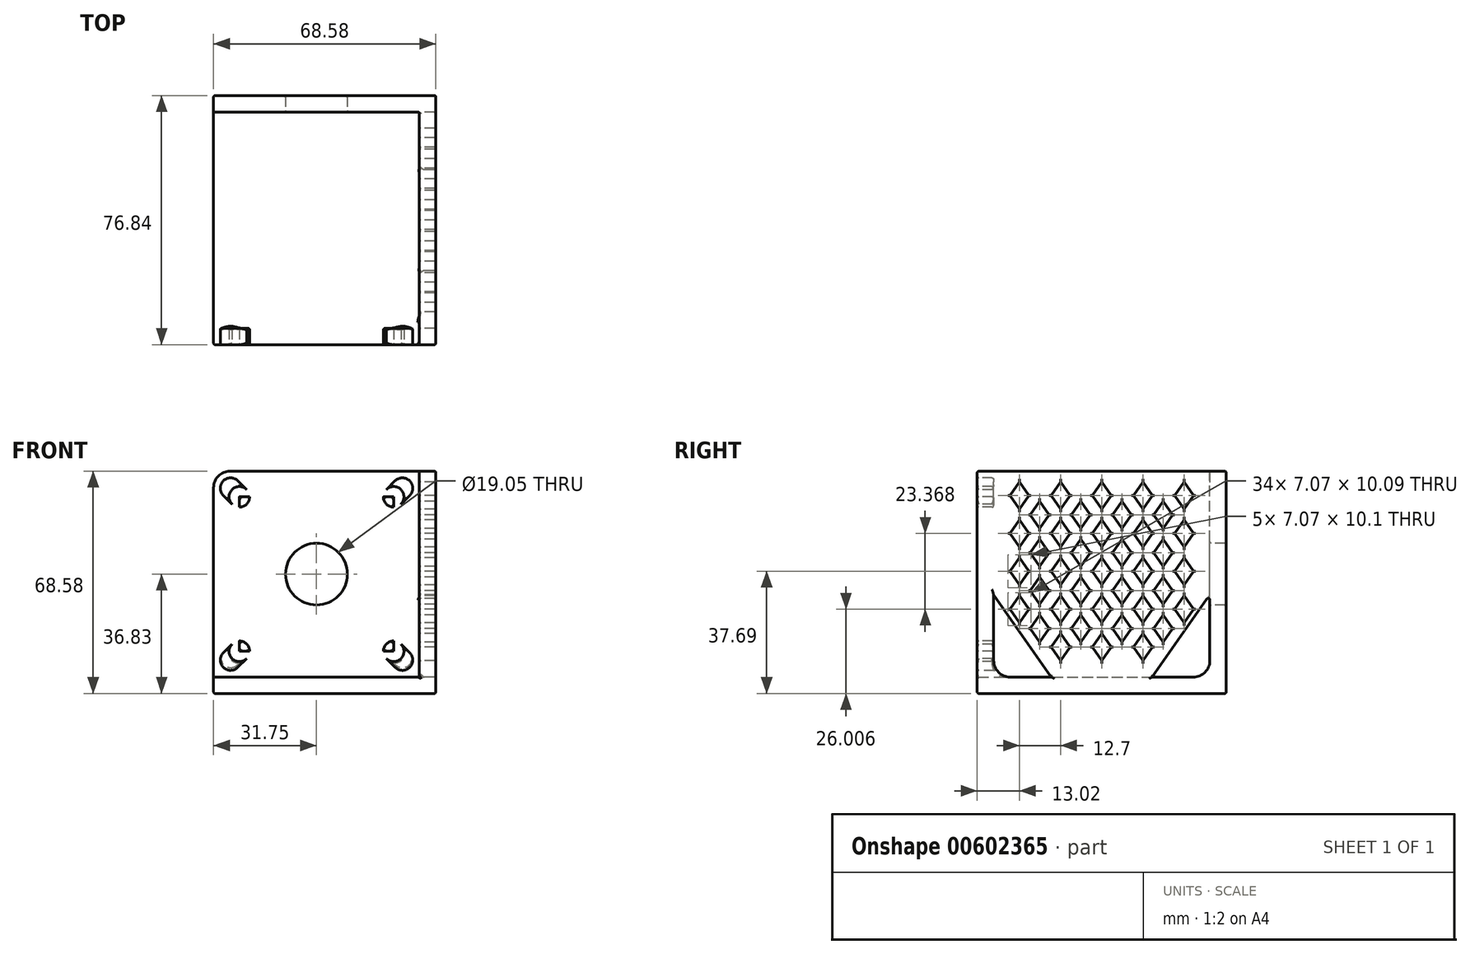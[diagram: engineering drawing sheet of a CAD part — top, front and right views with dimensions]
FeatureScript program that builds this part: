
annotation { "Feature Type Name" : "Feature", "Feature Type Description" : "" }
export const myFeature = defineFeature(function(context is Context, id is Id, definition is map)
    precondition{}
    {
        {
            var Q0;
            Q0=qCreatedBy(makeId("Right.planeOp"),FACE);
            var sketch = newSketch(context, id + "F0", { "sketchPlane" : qUnion([Q0])});
            skLineSegment(sketch, "E0", {"start": v(0, 0) * mm, "end": v(33.34, 0) * mm});
            skLineSegment(sketch, "E1", {"start": v(33.34, 0) * mm, "end": v(33.34, 63.5) * mm});
            skLineSegment(sketch, "E2", {"start": v(33.34, 63.5) * mm, "end": v(38.42, 63.5) * mm});
            skLineSegment(sketch, "E3", {"start": v(38.42, 63.5) * mm, "end": v(38.42, -5.08) * mm});
            skLineSegment(sketch, "E4", {"start": v(38.42, -5.08) * mm, "end": v(0, -5.08) * mm});
            skLineSegment(sketch, "E5", {"start": v(0, -5.08) * mm, "end": v(0, 0) * mm});
            skLineSegment(sketch, "E6.MirrorCS", {"start": v(-33.34, 0) * mm, "end": v(-33.34, 63.5) * mm});
            skLineSegment(sketch, "E7.MirrorCS", {"start": v(0, 0) * mm, "end": v(-33.34, 0) * mm});
            skLineSegment(sketch, "E8.MirrorCS", {"start": v(-38.42, -5.08) * mm, "end": v(0, -5.08) * mm});
            skLineSegment(sketch, "E9.MirrorCS", {"start": v(-38.42, 63.5) * mm, "end": v(-38.42, -5.08) * mm});
            skLineSegment(sketch, "E10.MirrorCS", {"start": v(-33.34, 63.5) * mm, "end": v(-38.42, 63.5) * mm});
            skSolve(sketch);
        }
        {
            var Q0;
            Q0=makeQuery(id+"F0.imprint","IMPRINT",FACE,{"disambiguationData":[TD([[makeQuery(id+"F0.imprint","IMPRINT",EDGE,{"derivedFrom":sQuery(id+"F0.wireOp",EDGE,"E0")}),-1.0]])]});
            var Q1;
            Q1=makeQuery(id+"F0.imprint","IMPRINT",FACE,{"disambiguationData":[TD([[makeQuery(id+"F0.imprint","IMPRINT",EDGE,{"derivedFrom":sQuery(id+"F0.wireOp",EDGE,"E5")}),1.0]])]});
            extrude(context, id + "F1", {"entities" : qUnion([Q0, Q1]), "endBound" : BoundingType.SYMMETRIC, "depth" : 63.5 * mm, "offsetDistance" : 25.4 * mm});
        }
        {
            var Q0;
            Q0=makeQuery(id+"F1.opExtrude","CAP_FACE",FACE,{"disambiguationData":[OSD([sQuery(id+"F0.wireOp",EDGE,"E0"),sQuery(id+"F0.wireOp",EDGE,"E1"),sQuery(id+"F0.wireOp",EDGE,"E2"),sQuery(id+"F0.wireOp",EDGE,"E3"),sQuery(id+"F0.wireOp",EDGE,"E4"),sQuery(id+"F0.wireOp",EDGE,"E6.MirrorCS"),sQuery(id+"F0.wireOp",EDGE,"E7.MirrorCS"),sQuery(id+"F0.wireOp",EDGE,"E8.MirrorCS"),sQuery(id+"F0.wireOp",EDGE,"E9.MirrorCS"),sQuery(id+"F0.wireOp",EDGE,"E10.MirrorCS")])],"isStart":false});
            var sketch = newSketch(context, id + "F2", { "sketchPlane" : qUnion([Q0])});
            skLineSegment(sketch, "E11.bottom", {"start": v(-38.42, 63.5) * mm, "end": v(38.42, 63.5) * mm});
            skLineSegment(sketch, "E11.top", {"start": v(-38.42, -5.08) * mm, "end": v(38.42, -5.08) * mm});
            skLineSegment(sketch, "E11.left", {"start": v(-38.42, 63.5) * mm, "end": v(-38.42, -5.08) * mm});
            skLineSegment(sketch, "E11.right", {"start": v(38.42, 63.5) * mm, "end": v(38.42, -5.08) * mm});
            skSolve(sketch);
        }
        {
            var Q0;
            {var subQ3=sQuery(id+"F0.wireOp",EDGE,"E1");var subQ6=makeQuery(id+"F1.opExtrude","CAP_EDGE",EDGE,{"disambiguationData":[OSD([subQ3])],"isStart":false});Q0=makeQuery(id+"F2.imprint","IMPRINT",FACE,{"disambiguationData":[TD([[makeQuery(id+"F2.imprint","IMPRINT",EDGE,{"derivedFrom":subQ6}),1.0]])]});}
            var Q1;
            Q1=makeQuery(id+"F2.imprint","IMPRINT",FACE,{"disambiguationData":[TD([[makeQuery(id+"F2.imprint","IMPRINT",EDGE,{"derivedFrom":sQuery(id+"F2.wireOp",EDGE,"E11.top")}),-1.0]])]});
            extrude(context, id + "F3", {"entities" : qUnion([Q0, Q1]), "operationType" : NewBodyOperationType.ADD, "depth" : 5.08 * mm, "offsetDistance" : 25.4 * mm});
        }
        {
            var Q0;
            Q0=makeQuery(id+"F1.opExtrude","SWEPT_EDGE",EDGE,{"disambiguationData":[OSD([sQuery(id+"F0.wireOp",EDGE,"E0"),sQuery(id+"F0.wireOp",EDGE,"E1")])]});
            var Q1;
            Q1=makeQuery(id+"F1.opExtrude","SWEPT_EDGE",EDGE,{"disambiguationData":[OSD([sQuery(id+"F0.wireOp",EDGE,"E6.MirrorCS"),sQuery(id+"F0.wireOp",EDGE,"E7.MirrorCS")])]});
            var Q2;
            Q2=makeQuery(id+"F1.opExtrude","CAP_EDGE",EDGE,{"disambiguationData":[OSD([sQuery(id+"F0.wireOp",EDGE,"E0"),sQuery(id+"F0.wireOp",EDGE,"E7.MirrorCS")])],"isStart":false});
            fillet(context, id + "F4", {"entities" : qUnion([Q0, Q1, Q2]), "radius" : 5.08 * mm, "tangentPropagation" : true, "allowEdgeOverflow" : false});
        }
        {
            var Q0;
            Q0=makeQuery(id+"F1.opExtrude","SWEPT_FACE",FACE,{"disambiguationData":[OSD([sQuery(id+"F0.wireOp",EDGE,"E9.MirrorCS")])]});
            var sketch = newSketch(context, id + "F5", { "sketchPlane" : qUnion([Q0])});
            skLineSegment(sketch, "E12.0", {"start": v(31.75, 0) * mm, "end": v(-31.75, 0) * mm});
            skLineSegment(sketch, "E13.0.0", {"start": v(-31.75, 63.5) * mm, "end": v(-31.75, -5.08) * mm});
            skLineSegment(sketch, "E13.0.1", {"start": v(-31.75, -5.08) * mm, "end": v(31.75, -5.08) * mm});
            skLineSegment(sketch, "E13.0.2", {"start": v(31.75, -5.08) * mm, "end": v(31.75, 63.5) * mm});
            skLineSegment(sketch, "E13.0.3", {"start": v(31.75, 63.5) * mm, "end": v(-31.75, 63.5) * mm});
            skPoint(sketch, "E14", {"position": v(0, 31.75) * mm});
            skCircle(sketch, "E15", {"center": v(0, 31.75) * mm, "radius": 19.84 * mm});
            skCircle(sketch, "E16", {"center": v(0, 31.75) * mm, "radius": 9.53 * mm});
            skSolve(sketch);
        }
        {
            var Q0;
            Q0=makeQuery(id+"F5.imprint","IMPRINT",FACE,{"disambiguationData":[TD([[makeQuery(id+"F5.imprint","IMPRINT",EDGE,{"derivedFrom":sQuery(id+"F5.wireOp",EDGE,"E16")}),1.0]])]});
            extrude(context, id + "F6", {"entities" : qUnion([Q0]), "operationType" : NewBodyOperationType.REMOVE, "endBound" : BoundingType.THROUGH_ALL, "oppositeDirection" : true, "depth" : 25.4 * mm, "offsetDistance" : 25.4 * mm});
        }
        {
            var Q0;
            Q0=makeQuery(id+"F5.imprint","IMPRINT",FACE,{"disambiguationData":[TD([[makeQuery(id+"F5.imprint","IMPRINT",EDGE,{"derivedFrom":sQuery(id+"F5.wireOp",EDGE,"E15")}),1.0]])]});
            extrude(context, id + "F7", {"entities" : qUnion([Q0]), "operationType" : NewBodyOperationType.REMOVE, "oppositeDirection" : true, "depth" : 25.4 * mm, "offsetDistance" : 25.4 * mm});
        }
        {
            var Q0;
            {var subQ2=sQuery(id+"F5.wireOp",EDGE,"E12.0");Q0=makeQuery(id+"F5.imprint","IMPRINT",FACE,{"disambiguationData":[TD([[makeQuery(id+"F5.imprint","IMPRINT",EDGE,{"derivedFrom":subQ2}),-1.0]])]});}
            var sketch = newSketch(context, id + "F8", { "sketchPlane" : qUnion([Q0])});
            skLineSegment(sketch, "E17", {"start": v(-23.81, 55.56) * mm, "end": v(23.81, 55.56) * mm});
            skPoint(sketch, "E18", {"position": v(0, 55.56) * mm});
            skLineSegment(sketch, "E19", {"start": v(-23.81, 55.56) * mm, "end": v(-23.81, 7.94) * mm});
            skPoint(sketch, "E20", {"position": v(-23.81, 31.75) * mm});
            skPoint(sketch, "E21.0", {"position": v(0, 31.75) * mm});
            skLineSegment(sketch, "E22", {"start": v(0, 31.75) * mm, "end": v(-34.13, 31.75) * mm});
            skLineSegment(sketch, "E23.MirrorCS", {"start": v(-23.81, 7.94) * mm, "end": v(23.81, 7.94) * mm});
            skLineSegment(sketch, "E24.MirrorCS", {"start": v(23.81, 55.56) * mm, "end": v(23.81, 7.94) * mm});
            skLineSegment(sketch, "E25", {"start": v(-23.81, 55.56) * mm, "end": v(-19.32, 51.07) * mm});
            skPoint(sketch, "E26", {"position": v(-19.32, 51.07) * mm});
            skLineSegment(sketch, "E27", {"start": v(-23.81, 55.56) * mm, "end": v(-26.5, 58.26) * mm});
            skLineSegment(sketch, "E28.MirrorCS", {"start": v(23.81, 55.56) * mm, "end": v(19.32, 51.07) * mm});
            skLineSegment(sketch, "E29.MirrorCS", {"start": v(23.81, 55.56) * mm, "end": v(26.5, 58.26) * mm});
            skLineSegment(sketch, "E30.MirrorCS", {"start": v(-23.81, 7.94) * mm, "end": v(-26.5, 5.24) * mm});
            skLineSegment(sketch, "E31.MirrorCS", {"start": v(-23.81, 7.94) * mm, "end": v(-19.32, 12.43) * mm});
            skLineSegment(sketch, "E32.MirrorCS", {"start": v(23.81, 7.94) * mm, "end": v(26.5, 5.24) * mm});
            skLineSegment(sketch, "E33.MirrorCS", {"start": v(23.81, 7.94) * mm, "end": v(19.32, 12.43) * mm});
            skArc(sketch, "E34.0.startCap", {"start": v(-21.57, 57.8) * mm, "mid": v(-21.57, 53.32) * mm, "end": v(-26.06, 53.32) * mm});
            skArc(sketch, "E34.0.endCap", {"start": v(-28.75, 56.01) * mm, "mid": v(-28.75, 60.5) * mm, "end": v(-24.26, 60.5) * mm});
            skLineSegment(sketch, "E34.0.left", {"start": v(-26.06, 53.32) * mm, "end": v(-28.75, 56.01) * mm});
            skLineSegment(sketch, "E34.0.right", {"start": v(-21.57, 57.8) * mm, "end": v(-24.26, 60.5) * mm});
            skArc(sketch, "E34.1.startCap", {"start": v(-26.06, 53.32) * mm, "mid": v(-26.06, 57.8) * mm, "end": v(-21.57, 57.8) * mm});
            skArc(sketch, "E34.1.endCap", {"start": v(-17.08, 53.32) * mm, "mid": v(-17.08, 48.83) * mm, "end": v(-21.57, 48.83) * mm});
            skLineSegment(sketch, "E34.1.left", {"start": v(-21.57, 57.8) * mm, "end": v(-17.08, 53.32) * mm});
            skLineSegment(sketch, "E34.1.right", {"start": v(-26.06, 53.32) * mm, "end": v(-21.57, 48.83) * mm});
            skArc(sketch, "E34.2.startCap", {"start": v(26.06, 53.32) * mm, "mid": v(21.57, 53.32) * mm, "end": v(21.57, 57.8) * mm});
            skArc(sketch, "E34.2.endCap", {"start": v(24.26, 60.5) * mm, "mid": v(28.75, 60.5) * mm, "end": v(28.75, 56.01) * mm});
            skLineSegment(sketch, "E34.2.left", {"start": v(21.57, 57.8) * mm, "end": v(24.26, 60.5) * mm});
            skLineSegment(sketch, "E34.2.right", {"start": v(26.06, 53.32) * mm, "end": v(28.75, 56.01) * mm});
            skArc(sketch, "E34.3.startCap", {"start": v(21.57, 57.8) * mm, "mid": v(26.06, 57.8) * mm, "end": v(26.06, 53.32) * mm});
            skArc(sketch, "E34.3.endCap", {"start": v(21.57, 48.83) * mm, "mid": v(17.08, 48.83) * mm, "end": v(17.08, 53.32) * mm});
            skLineSegment(sketch, "E34.3.left", {"start": v(26.06, 53.32) * mm, "end": v(21.57, 48.83) * mm});
            skLineSegment(sketch, "E34.3.right", {"start": v(21.57, 57.8) * mm, "end": v(17.08, 53.32) * mm});
            skArc(sketch, "E34.4.startCap", {"start": v(26.06, 10.18) * mm, "mid": v(26.06, 5.7) * mm, "end": v(21.57, 5.7) * mm});
            skArc(sketch, "E34.4.endCap", {"start": v(17.08, 10.18) * mm, "mid": v(17.08, 14.67) * mm, "end": v(21.57, 14.67) * mm});
            skLineSegment(sketch, "E34.4.left", {"start": v(21.57, 5.7) * mm, "end": v(17.08, 10.18) * mm});
            skLineSegment(sketch, "E34.4.right", {"start": v(26.06, 10.18) * mm, "end": v(21.57, 14.67) * mm});
            skArc(sketch, "E34.5.startCap", {"start": v(21.57, 5.7) * mm, "mid": v(21.57, 10.18) * mm, "end": v(26.06, 10.18) * mm});
            skArc(sketch, "E34.5.endCap", {"start": v(28.75, 7.49) * mm, "mid": v(28.75, 3) * mm, "end": v(24.26, 3) * mm});
            skLineSegment(sketch, "E34.5.left", {"start": v(26.06, 10.18) * mm, "end": v(28.75, 7.49) * mm});
            skLineSegment(sketch, "E34.5.right", {"start": v(21.57, 5.7) * mm, "end": v(24.26, 3) * mm});
            skArc(sketch, "E34.6.startCap", {"start": v(-21.57, 5.7) * mm, "mid": v(-26.06, 5.7) * mm, "end": v(-26.06, 10.18) * mm});
            skArc(sketch, "E34.6.endCap", {"start": v(-21.57, 14.67) * mm, "mid": v(-17.08, 14.67) * mm, "end": v(-17.08, 10.18) * mm});
            skLineSegment(sketch, "E34.6.left", {"start": v(-26.06, 10.18) * mm, "end": v(-21.57, 14.67) * mm});
            skLineSegment(sketch, "E34.6.right", {"start": v(-21.57, 5.7) * mm, "end": v(-17.08, 10.18) * mm});
            skArc(sketch, "E34.7.startCap", {"start": v(-26.06, 10.18) * mm, "mid": v(-21.57, 10.18) * mm, "end": v(-21.57, 5.7) * mm});
            skArc(sketch, "E34.7.endCap", {"start": v(-24.26, 3) * mm, "mid": v(-28.75, 3) * mm, "end": v(-28.75, 7.49) * mm});
            skLineSegment(sketch, "E34.7.left", {"start": v(-21.57, 5.7) * mm, "end": v(-24.26, 3) * mm});
            skLineSegment(sketch, "E34.7.right", {"start": v(-26.06, 10.18) * mm, "end": v(-28.75, 7.49) * mm});
            skSolve(sketch);
        }
        {
            var Q0;
            {var subQ1=sQuery(id+"F8.wireOp",EDGE,"E17");var subQ3=sQuery(id+"F8.wireOp",EDGE,"E34.0.startCap");var subQ4=makeQuery(id+"F8.imprint","INTERSECT",VERTEX,{"derivedFrom":[subQ1,subQ3]});Q0=makeQuery(id+"F8.imprint","IMPRINT",FACE,{"disambiguationData":[TD([[makeQuery(id+"F8.imprint","IMPRINT",EDGE,{"disambiguationData":[TD([[subQ4,1.0]])],"derivedFrom":subQ1}),1.0]])]});}
            var Q1;
            {var subQ1=sQuery(id+"F8.wireOp",EDGE,"E19");var subQ3=sQuery(id+"F8.wireOp",EDGE,"E34.0.startCap");var subQ4=makeQuery(id+"F8.imprint","INTERSECT",VERTEX,{"derivedFrom":[subQ1,subQ3]});Q1=makeQuery(id+"F8.imprint","IMPRINT",FACE,{"disambiguationData":[TD([[makeQuery(id+"F8.imprint","IMPRINT",EDGE,{"disambiguationData":[TD([[subQ4,1.0]])],"derivedFrom":subQ1}),-1.0]])]});}
            var Q2;
            {var subQ0=sQuery(id+"F8.wireOp",EDGE,"E25");var subQ3=sQuery(id+"F8.wireOp",EDGE,"E34.0.startCap");var subQ5=makeQuery(id+"F8.imprint","INTERSECT",VERTEX,{"derivedFrom":[subQ0,subQ3]});Q2=makeQuery(id+"F8.imprint","IMPRINT",FACE,{"disambiguationData":[TD([[makeQuery(id+"F8.imprint","IMPRINT",EDGE,{"disambiguationData":[TD([[subQ5,1.0]])],"derivedFrom":subQ3}),-1.0]])]});}
            var Q3;
            {var subQ0=sQuery(id+"F8.wireOp",EDGE,"E25");var subQ3=sQuery(id+"F8.wireOp",EDGE,"E34.0.startCap");var subQ5=makeQuery(id+"F8.imprint","INTERSECT",VERTEX,{"derivedFrom":[subQ0,subQ3]});Q3=makeQuery(id+"F8.imprint","IMPRINT",FACE,{"disambiguationData":[TD([[makeQuery(id+"F8.imprint","IMPRINT",EDGE,{"disambiguationData":[TD([[subQ5,-1.0]])],"derivedFrom":subQ3}),-1.0]])]});}
            var Q4;
            {var subQ7=sQuery(id+"F8.wireOp",EDGE,"E34.1.endCap");Q4=makeQuery(id+"F8.imprint","IMPRINT",FACE,{"disambiguationData":[TD([[makeQuery(id+"F8.imprint","IMPRINT",EDGE,{"derivedFrom":subQ7}),-1.0]])]});}
            var Q5;
            {var subQ0=sQuery(id+"F8.wireOp",EDGE,"E34.0.startCap");var subQ1=sQuery(id+"F8.wireOp",EDGE,"E17");var subQ2=makeQuery(id+"F8.imprint","INTERSECT",VERTEX,{"derivedFrom":[subQ1,subQ0]});Q5=makeQuery(id+"F8.imprint","IMPRINT",FACE,{"disambiguationData":[TD([[makeQuery(id+"F8.imprint","IMPRINT",EDGE,{"disambiguationData":[TD([[subQ2,-1.0]])],"derivedFrom":subQ1}),1.0]])]});}
            var Q6;
            {var subQ0=sQuery(id+"F8.wireOp",EDGE,"E34.0.startCap");var subQ1=sQuery(id+"F8.wireOp",EDGE,"E19");var subQ2=makeQuery(id+"F8.imprint","INTERSECT",VERTEX,{"derivedFrom":[subQ1,subQ0]});Q6=makeQuery(id+"F8.imprint","IMPRINT",FACE,{"disambiguationData":[TD([[makeQuery(id+"F8.imprint","IMPRINT",EDGE,{"disambiguationData":[TD([[subQ2,-1.0]])],"derivedFrom":subQ1}),-1.0]])]});}
            var Q7;
            Q7=makeQuery(id+"F8.imprint","IMPRINT",FACE,{"disambiguationData":[TD([[makeQuery(id+"F8.imprint","IMPRINT",EDGE,{"derivedFrom":sQuery(id+"F8.wireOp",EDGE,"E34.0.endCap")}),-1.0]])]});
            var Q8;
            Q8=makeQuery(id+"F8.imprint","IMPRINT",FACE,{"disambiguationData":[TD([[makeQuery(id+"F8.imprint","IMPRINT",EDGE,{"derivedFrom":sQuery(id+"F8.wireOp",EDGE,"E34.2.endCap")}),-1.0]])]});
            var Q9;
            {var subQ1=sQuery(id+"F8.wireOp",EDGE,"E24.MirrorCS");var subQ3=sQuery(id+"F8.wireOp",EDGE,"E34.2.startCap");var subQ4=makeQuery(id+"F8.imprint","INTERSECT",VERTEX,{"derivedFrom":[subQ1,subQ3]});Q9=makeQuery(id+"F8.imprint","IMPRINT",FACE,{"disambiguationData":[TD([[makeQuery(id+"F8.imprint","IMPRINT",EDGE,{"disambiguationData":[TD([[subQ4,1.0]])],"derivedFrom":subQ1}),1.0]])]});}
            var Q10;
            {var subQ1=sQuery(id+"F8.wireOp",EDGE,"E17");var subQ3=sQuery(id+"F8.wireOp",EDGE,"E34.2.startCap");var subQ4=makeQuery(id+"F8.imprint","INTERSECT",VERTEX,{"derivedFrom":[subQ1,subQ3]});Q10=makeQuery(id+"F8.imprint","IMPRINT",FACE,{"disambiguationData":[TD([[makeQuery(id+"F8.imprint","IMPRINT",EDGE,{"disambiguationData":[TD([[subQ4,-1.0]])],"derivedFrom":subQ1}),1.0]])]});}
            var Q11;
            {var subQ0=sQuery(id+"F8.wireOp",EDGE,"E28.MirrorCS");var subQ3=sQuery(id+"F8.wireOp",EDGE,"E34.2.startCap");var subQ5=makeQuery(id+"F8.imprint","INTERSECT",VERTEX,{"derivedFrom":[subQ0,subQ3]});Q11=makeQuery(id+"F8.imprint","IMPRINT",FACE,{"disambiguationData":[TD([[makeQuery(id+"F8.imprint","IMPRINT",EDGE,{"disambiguationData":[TD([[subQ5,-1.0]])],"derivedFrom":subQ3}),-1.0]])]});}
            var Q12;
            {var subQ5=sQuery(id+"F8.wireOp",EDGE,"E34.3.endCap");Q12=makeQuery(id+"F8.imprint","IMPRINT",FACE,{"disambiguationData":[TD([[makeQuery(id+"F8.imprint","IMPRINT",EDGE,{"derivedFrom":subQ5}),-1.0]])]});}
            var Q13;
            {var subQ0=sQuery(id+"F8.wireOp",EDGE,"E34.2.startCap");var subQ1=sQuery(id+"F8.wireOp",EDGE,"E24.MirrorCS");var subQ2=makeQuery(id+"F8.imprint","INTERSECT",VERTEX,{"derivedFrom":[subQ1,subQ0]});Q13=makeQuery(id+"F8.imprint","IMPRINT",FACE,{"disambiguationData":[TD([[makeQuery(id+"F8.imprint","IMPRINT",EDGE,{"disambiguationData":[TD([[subQ2,-1.0]])],"derivedFrom":subQ1}),1.0]])]});}
            var Q14;
            {var subQ0=sQuery(id+"F8.wireOp",EDGE,"E34.3.right");var subQ1=sQuery(id+"F8.wireOp",EDGE,"E17");var subQ2=makeQuery(id+"F8.imprint","INTERSECT",VERTEX,{"derivedFrom":[subQ1,subQ0]});Q14=makeQuery(id+"F8.imprint","IMPRINT",FACE,{"disambiguationData":[TD([[makeQuery(id+"F8.imprint","IMPRINT",EDGE,{"disambiguationData":[TD([[subQ2,-1.0]])],"derivedFrom":subQ1}),1.0]])]});}
            var Q15;
            {var subQ0=sQuery(id+"F8.wireOp",EDGE,"E28.MirrorCS");var subQ3=sQuery(id+"F8.wireOp",EDGE,"E34.2.startCap");var subQ5=makeQuery(id+"F8.imprint","INTERSECT",VERTEX,{"derivedFrom":[subQ0,subQ3]});Q15=makeQuery(id+"F8.imprint","IMPRINT",FACE,{"disambiguationData":[TD([[makeQuery(id+"F8.imprint","IMPRINT",EDGE,{"disambiguationData":[TD([[subQ5,1.0]])],"derivedFrom":subQ3}),-1.0]])]});}
            var Q16;
            {var subQ0=sQuery(id+"F8.wireOp",EDGE,"E34.4.left");var subQ1=sQuery(id+"F8.wireOp",EDGE,"E23.MirrorCS");var subQ2=makeQuery(id+"F8.imprint","INTERSECT",VERTEX,{"derivedFrom":[subQ1,subQ0]});Q16=makeQuery(id+"F8.imprint","IMPRINT",FACE,{"disambiguationData":[TD([[makeQuery(id+"F8.imprint","IMPRINT",EDGE,{"disambiguationData":[TD([[subQ2,-1.0]])],"derivedFrom":subQ1}),-1.0]])]});}
            var Q17;
            {var subQ0=sQuery(id+"F8.wireOp",EDGE,"E34.4.right");var subQ1=sQuery(id+"F8.wireOp",EDGE,"E24.MirrorCS");var subQ2=makeQuery(id+"F8.imprint","INTERSECT",VERTEX,{"derivedFrom":[subQ1,subQ0]});Q17=makeQuery(id+"F8.imprint","IMPRINT",FACE,{"disambiguationData":[TD([[makeQuery(id+"F8.imprint","IMPRINT",EDGE,{"disambiguationData":[TD([[subQ2,-1.0]])],"derivedFrom":subQ1}),1.0]])]});}
            var Q18;
            Q18=makeQuery(id+"F8.imprint","IMPRINT",FACE,{"disambiguationData":[TD([[makeQuery(id+"F8.imprint","IMPRINT",EDGE,{"derivedFrom":sQuery(id+"F8.wireOp",EDGE,"E34.5.endCap")}),-1.0]])]});
            var Q19;
            {var subQ1=sQuery(id+"F8.wireOp",EDGE,"E24.MirrorCS");var subQ3=sQuery(id+"F8.wireOp",EDGE,"E34.5.startCap");var subQ4=makeQuery(id+"F8.imprint","INTERSECT",VERTEX,{"derivedFrom":[subQ1,subQ3]});Q19=makeQuery(id+"F8.imprint","IMPRINT",FACE,{"disambiguationData":[TD([[makeQuery(id+"F8.imprint","IMPRINT",EDGE,{"disambiguationData":[TD([[subQ4,-1.0]])],"derivedFrom":subQ1}),1.0]])]});}
            var Q20;
            {var subQ1=sQuery(id+"F8.wireOp",EDGE,"E23.MirrorCS");var subQ3=sQuery(id+"F8.wireOp",EDGE,"E34.5.startCap");var subQ4=makeQuery(id+"F8.imprint","INTERSECT",VERTEX,{"derivedFrom":[subQ1,subQ3]});Q20=makeQuery(id+"F8.imprint","IMPRINT",FACE,{"disambiguationData":[TD([[makeQuery(id+"F8.imprint","IMPRINT",EDGE,{"disambiguationData":[TD([[subQ4,-1.0]])],"derivedFrom":subQ1}),-1.0]])]});}
            var Q21;
            {var subQ0=sQuery(id+"F8.wireOp",EDGE,"E33.MirrorCS");var subQ3=sQuery(id+"F8.wireOp",EDGE,"E34.5.startCap");var subQ5=makeQuery(id+"F8.imprint","INTERSECT",VERTEX,{"derivedFrom":[subQ0,subQ3]});Q21=makeQuery(id+"F8.imprint","IMPRINT",FACE,{"disambiguationData":[TD([[makeQuery(id+"F8.imprint","IMPRINT",EDGE,{"disambiguationData":[TD([[subQ5,1.0]])],"derivedFrom":subQ3}),-1.0]])]});}
            var Q22;
            {var subQ0=sQuery(id+"F8.wireOp",EDGE,"E33.MirrorCS");var subQ3=sQuery(id+"F8.wireOp",EDGE,"E34.5.startCap");var subQ5=makeQuery(id+"F8.imprint","INTERSECT",VERTEX,{"derivedFrom":[subQ0,subQ3]});Q22=makeQuery(id+"F8.imprint","IMPRINT",FACE,{"disambiguationData":[TD([[makeQuery(id+"F8.imprint","IMPRINT",EDGE,{"disambiguationData":[TD([[subQ5,-1.0]])],"derivedFrom":subQ3}),-1.0]])]});}
            var Q23;
            {var subQ1=sQuery(id+"F8.wireOp",EDGE,"E34.4.endCap");Q23=makeQuery(id+"F8.imprint","IMPRINT",FACE,{"disambiguationData":[TD([[makeQuery(id+"F8.imprint","IMPRINT",EDGE,{"derivedFrom":subQ1}),-1.0]])]});}
            var Q24;
            {var subQ1=sQuery(id+"F8.wireOp",EDGE,"E34.6.endCap");Q24=makeQuery(id+"F8.imprint","IMPRINT",FACE,{"disambiguationData":[TD([[makeQuery(id+"F8.imprint","IMPRINT",EDGE,{"derivedFrom":subQ1}),-1.0]])]});}
            var Q25;
            {var subQ0=sQuery(id+"F8.wireOp",EDGE,"E31.MirrorCS");var subQ3=sQuery(id+"F8.wireOp",EDGE,"E34.7.startCap");var subQ5=makeQuery(id+"F8.imprint","INTERSECT",VERTEX,{"derivedFrom":[subQ0,subQ3]});Q25=makeQuery(id+"F8.imprint","IMPRINT",FACE,{"disambiguationData":[TD([[makeQuery(id+"F8.imprint","IMPRINT",EDGE,{"disambiguationData":[TD([[subQ5,1.0]])],"derivedFrom":subQ3}),-1.0]])]});}
            var Q26;
            {var subQ1=sQuery(id+"F8.wireOp",EDGE,"E23.MirrorCS");var subQ3=sQuery(id+"F8.wireOp",EDGE,"E34.7.startCap");var subQ4=makeQuery(id+"F8.imprint","INTERSECT",VERTEX,{"derivedFrom":[subQ1,subQ3]});Q26=makeQuery(id+"F8.imprint","IMPRINT",FACE,{"disambiguationData":[TD([[makeQuery(id+"F8.imprint","IMPRINT",EDGE,{"disambiguationData":[TD([[subQ4,1.0]])],"derivedFrom":subQ1}),-1.0]])]});}
            var Q27;
            {var subQ1=sQuery(id+"F8.wireOp",EDGE,"E19");var subQ3=sQuery(id+"F8.wireOp",EDGE,"E34.7.startCap");var subQ4=makeQuery(id+"F8.imprint","INTERSECT",VERTEX,{"derivedFrom":[subQ1,subQ3]});Q27=makeQuery(id+"F8.imprint","IMPRINT",FACE,{"disambiguationData":[TD([[makeQuery(id+"F8.imprint","IMPRINT",EDGE,{"disambiguationData":[TD([[subQ4,-1.0]])],"derivedFrom":subQ1}),-1.0]])]});}
            var Q28;
            Q28=makeQuery(id+"F8.imprint","IMPRINT",FACE,{"disambiguationData":[TD([[makeQuery(id+"F8.imprint","IMPRINT",EDGE,{"derivedFrom":sQuery(id+"F8.wireOp",EDGE,"E34.7.endCap")}),-1.0]])]});
            var Q29;
            {var subQ0=sQuery(id+"F8.wireOp",EDGE,"E34.7.startCap");var subQ1=sQuery(id+"F8.wireOp",EDGE,"E23.MirrorCS");var subQ2=makeQuery(id+"F8.imprint","INTERSECT",VERTEX,{"derivedFrom":[subQ1,subQ0]});Q29=makeQuery(id+"F8.imprint","IMPRINT",FACE,{"disambiguationData":[TD([[makeQuery(id+"F8.imprint","IMPRINT",EDGE,{"disambiguationData":[TD([[subQ2,-1.0]])],"derivedFrom":subQ1}),-1.0]])]});}
            var Q30;
            {var subQ0=sQuery(id+"F8.wireOp",EDGE,"E34.6.left");var subQ1=sQuery(id+"F8.wireOp",EDGE,"E19");var subQ2=makeQuery(id+"F8.imprint","INTERSECT",VERTEX,{"derivedFrom":[subQ1,subQ0]});Q30=makeQuery(id+"F8.imprint","IMPRINT",FACE,{"disambiguationData":[TD([[makeQuery(id+"F8.imprint","IMPRINT",EDGE,{"disambiguationData":[TD([[subQ2,-1.0]])],"derivedFrom":subQ1}),-1.0]])]});}
            var Q31;
            {var subQ0=sQuery(id+"F8.wireOp",EDGE,"E31.MirrorCS");var subQ3=sQuery(id+"F8.wireOp",EDGE,"E34.7.startCap");var subQ5=makeQuery(id+"F8.imprint","INTERSECT",VERTEX,{"derivedFrom":[subQ0,subQ3]});Q31=makeQuery(id+"F8.imprint","IMPRINT",FACE,{"disambiguationData":[TD([[makeQuery(id+"F8.imprint","IMPRINT",EDGE,{"disambiguationData":[TD([[subQ5,-1.0]])],"derivedFrom":subQ3}),-1.0]])]});}
            extrude(context, id + "F9", {"entities" : qUnion([Q0, Q1, Q2, Q3, Q4, Q5, Q6, Q7, Q8, Q9, Q10, Q11, Q12, Q13, Q14, Q15, Q16, Q17, Q18, Q19, Q20, Q21, Q22, Q23, Q24, Q25, Q26, Q27, Q28, Q29, Q30, Q31]), "operationType" : NewBodyOperationType.REMOVE, "oppositeDirection" : true, "depth" : 25.4 * mm, "offsetDistance" : 25.4 * mm});
        }
        {
            var Q0;
            Q0=makeQuery(id+"F3.opExtrude","CAP_FACE",FACE,{"disambiguationData":[OSD([sQuery(id+"F2.wireOp",EDGE,"E11.bottom"),sQuery(id+"F2.wireOp",EDGE,"E11.top"),sQuery(id+"F2.wireOp",EDGE,"E11.left"),sQuery(id+"F2.wireOp",EDGE,"E11.right")])],"isStart":true});
            var sketch = newSketch(context, id + "F10", { "sketchPlane" : qUnion([Q0])});
            skArc(sketch, "E35.0.0", {"start": v(28.26, 0) * mm, "mid": v(31.85, 1.49) * mm, "end": v(33.34, 5.08) * mm});
            skLineSegment(sketch, "E35.0.1", {"start": v(-33.34, 5.08) * mm, "end": v(33.34, 5.08) * mm});
            skArc(sketch, "E35.0.2", {"start": v(-33.34, 5.08) * mm, "mid": v(-31.85, 1.49) * mm, "end": v(-28.26, 0) * mm});
            skLineSegment(sketch, "E35.0.3", {"start": v(-28.26, 0) * mm, "end": v(-15.56, 0) * mm});
            skLineSegment(sketch, "E36.0.0", {"start": v(33.34, 5.08) * mm, "end": v(33.34, 63) * mm});
            skLineSegment(sketch, "E36.0.1", {"start": v(33.34, 63) * mm, "end": v(-33.34, 63) * mm});
            skLineSegment(sketch, "E36.0.2", {"start": v(-33.34, 63) * mm, "end": v(-33.34, 25.4) * mm});
            skLineSegment(sketch, "E37", {"start": v(-33.34, 25.4) * mm, "end": v(-33.34, 5.08) * mm});
            skLineSegment(sketch, "E38", {"start": v(-15.56, 0) * mm, "end": v(28.26, 0) * mm});
            skLineSegment(sketch, "E39", {"start": v(-15.56, 0) * mm, "end": v(-33.34, 25.4) * mm});
            skLineSegment(sketch, "E40.MirrorCS", {"start": v(15.56, 0) * mm, "end": v(33.34, 25.4) * mm});
            skSolve(sketch);
        }
        {
            var Q0;
            {var subQ1=sQuery(id+"F10.wireOp",EDGE,"E36.0.0");var subQ3=sQuery(id+"F10.wireOp",EDGE,"E40.MirrorCS");var subQ4=makeQuery(id+"F10.imprint","INTERSECT",VERTEX,{"derivedFrom":[subQ1,subQ3]});Q0=makeQuery(id+"F10.imprint","IMPRINT",FACE,{"disambiguationData":[TD([[makeQuery(id+"F10.imprint","IMPRINT",EDGE,{"disambiguationData":[TD([[subQ4,1.0]])],"derivedFrom":subQ3}),-1.0]])]});}
            var Q1;
            {var subQ0=sQuery(id+"F10.wireOp",EDGE,"E37");Q1=makeQuery(id+"F10.imprint","IMPRINT",FACE,{"disambiguationData":[TD([[makeQuery(id+"F10.imprint","IMPRINT",EDGE,{"derivedFrom":subQ0}),-1.0]])]});}
            var Q2;
            {var subQ0=sQuery(id+"F10.wireOp",EDGE,"E35.0.2");Q2=makeQuery(id+"F10.imprint","IMPRINT",FACE,{"disambiguationData":[TD([[makeQuery(id+"F10.imprint","IMPRINT",EDGE,{"derivedFrom":subQ0}),1.0]])]});}
            var Q3;
            {var subQ0=sQuery(id+"F10.wireOp",EDGE,"E35.0.0");Q3=makeQuery(id+"F10.imprint","IMPRINT",FACE,{"disambiguationData":[TD([[makeQuery(id+"F10.imprint","IMPRINT",EDGE,{"derivedFrom":subQ0}),1.0]])]});}
            extrude(context, id + "F11", {"entities" : qUnion([Q0, Q1, Q2, Q3]), "operationType" : NewBodyOperationType.REMOVE, "endBound" : BoundingType.SYMMETRIC, "oppositeDirection" : true, "depth" : 25.4 * mm, "offsetDistance" : 25.4 * mm});
        }
        {
            var Q0;
            Q0=makeQuery(id+"F3.opExtrude","CAP_FACE",FACE,{"disambiguationData":[OSD([sQuery(id+"F2.wireOp",EDGE,"E11.bottom"),sQuery(id+"F2.wireOp",EDGE,"E11.top"),sQuery(id+"F2.wireOp",EDGE,"E11.left"),sQuery(id+"F2.wireOp",EDGE,"E11.right")])],"isStart":true});
            var sketch = newSketch(context, id + "F12", { "sketchPlane" : qUnion([Q0])});
            skLineSegment(sketch, "E41.2.4.0", {"start": v(25.4, 60.14) * mm, "end": v(22.49, 55.98) * mm});
            skLineSegment(sketch, "E41.2.4.1", {"start": v(25.4, 60.14) * mm, "end": v(28.31, 55.98) * mm});
            skLineSegment(sketch, "E41.2.4.2", {"start": v(25.4, 51.82) * mm, "end": v(28.31, 55.98) * mm});
            skLineSegment(sketch, "E41.2.4.3", {"start": v(25.4, 51.82) * mm, "end": v(22.49, 55.98) * mm});
            skLineSegment(sketch, "E42.0.1.0", {"start": v(25.4, 48.46) * mm, "end": v(22.49, 44.3) * mm});
            skLineSegment(sketch, "E42.0.1.1", {"start": v(25.4, 48.46) * mm, "end": v(28.31, 44.3) * mm});
            skLineSegment(sketch, "E42.0.1.2", {"start": v(25.4, 40.13) * mm, "end": v(28.31, 44.3) * mm});
            skLineSegment(sketch, "E42.0.1.3", {"start": v(25.4, 40.13) * mm, "end": v(22.49, 44.3) * mm});
            skLineSegment(sketch, "E42.0.2.0", {"start": v(25.4, 36.77) * mm, "end": v(22.49, 32.6) * mm});
            skLineSegment(sketch, "E42.0.2.1", {"start": v(25.4, 36.77) * mm, "end": v(28.31, 32.6) * mm});
            skLineSegment(sketch, "E42.0.2.2", {"start": v(25.4, 28.45) * mm, "end": v(28.31, 32.6) * mm});
            skLineSegment(sketch, "E42.0.2.3", {"start": v(25.4, 28.45) * mm, "end": v(22.49, 32.6) * mm});
            skLineSegment(sketch, "E42.0.3.0", {"start": v(25.4, 25.09) * mm, "end": v(22.49, 20.93) * mm});
            skLineSegment(sketch, "E42.0.3.1", {"start": v(25.4, 25.09) * mm, "end": v(28.31, 20.93) * mm});
            skLineSegment(sketch, "E42.0.3.2", {"start": v(25.4, 16.76) * mm, "end": v(28.31, 20.93) * mm});
            skLineSegment(sketch, "E42.0.3.3", {"start": v(25.4, 16.76) * mm, "end": v(22.49, 20.93) * mm});
            skLineSegment(sketch, "E42.0.4.0", {"start": v(19.11, 19.14) * mm, "end": v(16.2, 14.98) * mm});
            skLineSegment(sketch, "E42.0.4.1", {"start": v(19.11, 19.14) * mm, "end": v(22.03, 14.98) * mm});
            skLineSegment(sketch, "E42.0.4.2", {"start": v(19.11, 10.82) * mm, "end": v(22.03, 14.98) * mm});
            skLineSegment(sketch, "E42.0.4.3", {"start": v(19.11, 10.82) * mm, "end": v(16.2, 14.98) * mm});
            skLineSegment(sketch, "E42.1.0.0", {"start": v(12.7, 60.14) * mm, "end": v(9.79, 55.98) * mm});
            skLineSegment(sketch, "E42.1.0.1", {"start": v(12.7, 60.14) * mm, "end": v(15.61, 55.98) * mm});
            skLineSegment(sketch, "E42.1.0.2", {"start": v(12.7, 51.82) * mm, "end": v(15.61, 55.98) * mm});
            skLineSegment(sketch, "E42.1.0.3", {"start": v(12.7, 51.82) * mm, "end": v(9.79, 55.98) * mm});
            skLineSegment(sketch, "E42.1.1.0", {"start": v(12.7, 48.46) * mm, "end": v(9.79, 44.3) * mm});
            skLineSegment(sketch, "E42.1.1.1", {"start": v(12.7, 48.46) * mm, "end": v(15.61, 44.3) * mm});
            skLineSegment(sketch, "E42.1.1.2", {"start": v(12.7, 40.13) * mm, "end": v(15.61, 44.3) * mm});
            skLineSegment(sketch, "E42.1.1.3", {"start": v(12.7, 40.13) * mm, "end": v(9.79, 44.3) * mm});
            skLineSegment(sketch, "E42.1.2.0", {"start": v(12.7, 36.77) * mm, "end": v(9.79, 32.6) * mm});
            skLineSegment(sketch, "E42.1.2.1", {"start": v(12.7, 36.77) * mm, "end": v(15.61, 32.6) * mm});
            skLineSegment(sketch, "E42.1.2.2", {"start": v(12.7, 28.45) * mm, "end": v(15.61, 32.6) * mm});
            skLineSegment(sketch, "E42.1.2.3", {"start": v(12.7, 28.45) * mm, "end": v(9.79, 32.6) * mm});
            skLineSegment(sketch, "E42.1.3.0", {"start": v(12.7, 25.09) * mm, "end": v(9.79, 20.93) * mm});
            skLineSegment(sketch, "E42.1.3.1", {"start": v(12.7, 25.09) * mm, "end": v(15.61, 20.93) * mm});
            skLineSegment(sketch, "E42.1.3.2", {"start": v(12.7, 16.76) * mm, "end": v(15.61, 20.93) * mm});
            skLineSegment(sketch, "E42.1.3.3", {"start": v(12.7, 16.76) * mm, "end": v(9.79, 20.93) * mm});
            skLineSegment(sketch, "E42.1.4.0", {"start": v(12.7, 13.4) * mm, "end": v(9.79, 9.24) * mm});
            skLineSegment(sketch, "E42.1.4.1", {"start": v(12.7, 13.4) * mm, "end": v(15.61, 9.24) * mm});
            skLineSegment(sketch, "E42.1.4.2", {"start": v(12.7, 5.08) * mm, "end": v(15.61, 9.24) * mm});
            skLineSegment(sketch, "E42.1.4.3", {"start": v(12.7, 5.08) * mm, "end": v(9.79, 9.24) * mm});
            skLineSegment(sketch, "E42.2.0.0", {"start": v(0, 60.14) * mm, "end": v(-2.91, 55.98) * mm});
            skLineSegment(sketch, "E42.2.0.1", {"start": v(0, 60.14) * mm, "end": v(2.91, 55.98) * mm});
            skLineSegment(sketch, "E42.2.0.2", {"start": v(0, 51.82) * mm, "end": v(2.91, 55.98) * mm});
            skLineSegment(sketch, "E42.2.0.3", {"start": v(0, 51.82) * mm, "end": v(-2.91, 55.98) * mm});
            skLineSegment(sketch, "E42.2.1.0", {"start": v(0, 48.46) * mm, "end": v(-2.91, 44.3) * mm});
            skLineSegment(sketch, "E42.2.1.1", {"start": v(0, 48.46) * mm, "end": v(2.91, 44.3) * mm});
            skLineSegment(sketch, "E42.2.1.2", {"start": v(0, 40.13) * mm, "end": v(2.91, 44.3) * mm});
            skLineSegment(sketch, "E42.2.1.3", {"start": v(0, 40.13) * mm, "end": v(-2.91, 44.3) * mm});
            skLineSegment(sketch, "E42.2.2.0", {"start": v(0, 36.77) * mm, "end": v(-2.91, 32.6) * mm});
            skLineSegment(sketch, "E42.2.2.1", {"start": v(0, 36.77) * mm, "end": v(2.91, 32.6) * mm});
            skLineSegment(sketch, "E42.2.2.2", {"start": v(0, 28.45) * mm, "end": v(2.91, 32.6) * mm});
            skLineSegment(sketch, "E42.2.2.3", {"start": v(0, 28.45) * mm, "end": v(-2.91, 32.6) * mm});
            skLineSegment(sketch, "E42.2.3.0", {"start": v(0, 25.09) * mm, "end": v(-2.91, 20.93) * mm});
            skLineSegment(sketch, "E42.2.3.1", {"start": v(0, 25.09) * mm, "end": v(2.91, 20.93) * mm});
            skLineSegment(sketch, "E42.2.3.2", {"start": v(0, 16.76) * mm, "end": v(2.91, 20.93) * mm});
            skLineSegment(sketch, "E42.2.3.3", {"start": v(0, 16.76) * mm, "end": v(-2.91, 20.93) * mm});
            skLineSegment(sketch, "E42.2.4.0", {"start": v(0, 13.4) * mm, "end": v(-2.91, 9.24) * mm});
            skLineSegment(sketch, "E42.2.4.1", {"start": v(0, 13.4) * mm, "end": v(2.91, 9.24) * mm});
            skLineSegment(sketch, "E42.2.4.2", {"start": v(0, 5.08) * mm, "end": v(2.91, 9.24) * mm});
            skLineSegment(sketch, "E42.2.4.3", {"start": v(0, 5.08) * mm, "end": v(-2.91, 9.24) * mm});
            skLineSegment(sketch, "E42.3.0.0", {"start": v(-12.7, 60.14) * mm, "end": v(-15.61, 55.98) * mm});
            skLineSegment(sketch, "E42.3.0.1", {"start": v(-12.7, 60.14) * mm, "end": v(-9.79, 55.98) * mm});
            skLineSegment(sketch, "E42.3.0.2", {"start": v(-12.7, 51.82) * mm, "end": v(-9.79, 55.98) * mm});
            skLineSegment(sketch, "E42.3.0.3", {"start": v(-12.7, 51.82) * mm, "end": v(-15.61, 55.98) * mm});
            skLineSegment(sketch, "E42.3.1.0", {"start": v(-12.7, 48.46) * mm, "end": v(-15.61, 44.3) * mm});
            skLineSegment(sketch, "E42.3.1.1", {"start": v(-12.7, 48.46) * mm, "end": v(-9.79, 44.3) * mm});
            skLineSegment(sketch, "E42.3.1.2", {"start": v(-12.7, 40.13) * mm, "end": v(-9.79, 44.3) * mm});
            skLineSegment(sketch, "E42.3.1.3", {"start": v(-12.7, 40.13) * mm, "end": v(-15.61, 44.3) * mm});
            skLineSegment(sketch, "E42.3.2.0", {"start": v(-12.7, 36.77) * mm, "end": v(-15.61, 32.6) * mm});
            skLineSegment(sketch, "E42.3.2.1", {"start": v(-12.7, 36.77) * mm, "end": v(-9.79, 32.6) * mm});
            skLineSegment(sketch, "E42.3.2.2", {"start": v(-12.7, 28.45) * mm, "end": v(-9.79, 32.6) * mm});
            skLineSegment(sketch, "E42.3.2.3", {"start": v(-12.7, 28.45) * mm, "end": v(-15.61, 32.6) * mm});
            skLineSegment(sketch, "E42.3.3.0", {"start": v(-12.7, 25.09) * mm, "end": v(-15.61, 20.93) * mm});
            skLineSegment(sketch, "E42.3.3.1", {"start": v(-12.7, 25.09) * mm, "end": v(-9.79, 20.93) * mm});
            skLineSegment(sketch, "E42.3.3.2", {"start": v(-12.7, 16.76) * mm, "end": v(-9.79, 20.93) * mm});
            skLineSegment(sketch, "E42.3.3.3", {"start": v(-12.7, 16.76) * mm, "end": v(-15.61, 20.93) * mm});
            skLineSegment(sketch, "E42.3.4.0", {"start": v(-12.7, 13.4) * mm, "end": v(-15.61, 9.24) * mm});
            skLineSegment(sketch, "E42.3.4.1", {"start": v(-12.7, 13.4) * mm, "end": v(-9.79, 9.24) * mm});
            skLineSegment(sketch, "E42.3.4.2", {"start": v(-12.7, 5.08) * mm, "end": v(-9.79, 9.24) * mm});
            skLineSegment(sketch, "E42.3.4.3", {"start": v(-12.7, 5.08) * mm, "end": v(-15.61, 9.24) * mm});
            skLineSegment(sketch, "E42.4.0.0", {"start": v(-25.4, 60.14) * mm, "end": v(-28.31, 55.98) * mm});
            skLineSegment(sketch, "E42.4.0.1", {"start": v(-25.4, 60.14) * mm, "end": v(-22.49, 55.98) * mm});
            skLineSegment(sketch, "E42.4.0.2", {"start": v(-25.4, 51.82) * mm, "end": v(-22.49, 55.98) * mm});
            skLineSegment(sketch, "E42.4.0.3", {"start": v(-25.4, 51.82) * mm, "end": v(-28.31, 55.98) * mm});
            skLineSegment(sketch, "E42.4.1.0", {"start": v(-25.4, 48.46) * mm, "end": v(-28.31, 44.3) * mm});
            skLineSegment(sketch, "E42.4.1.1", {"start": v(-25.4, 48.46) * mm, "end": v(-22.49, 44.3) * mm});
            skLineSegment(sketch, "E42.4.1.2", {"start": v(-25.4, 40.13) * mm, "end": v(-22.49, 44.3) * mm});
            skLineSegment(sketch, "E42.4.1.3", {"start": v(-25.4, 40.13) * mm, "end": v(-28.31, 44.3) * mm});
            skLineSegment(sketch, "E42.4.2.0", {"start": v(-25.4, 36.77) * mm, "end": v(-28.31, 32.6) * mm});
            skLineSegment(sketch, "E42.4.2.1", {"start": v(-25.4, 36.77) * mm, "end": v(-22.49, 32.6) * mm});
            skLineSegment(sketch, "E42.4.2.2", {"start": v(-25.4, 28.45) * mm, "end": v(-22.49, 32.6) * mm});
            skLineSegment(sketch, "E42.4.2.3", {"start": v(-25.4, 28.45) * mm, "end": v(-28.31, 32.6) * mm});
            skLineSegment(sketch, "E42.4.3.0", {"start": v(-25.4, 25.09) * mm, "end": v(-28.31, 20.93) * mm});
            skLineSegment(sketch, "E42.4.3.1", {"start": v(-25.4, 25.09) * mm, "end": v(-22.49, 20.93) * mm});
            skLineSegment(sketch, "E42.4.3.2", {"start": v(-25.4, 16.76) * mm, "end": v(-22.49, 20.93) * mm});
            skLineSegment(sketch, "E42.4.3.3", {"start": v(-25.4, 16.76) * mm, "end": v(-28.31, 20.93) * mm});
            skLineSegment(sketch, "E42.direction1", {"start": v(22.49, 55.98) * mm, "end": v(9.79, 55.98) * mm, "construction": true});
            skLineSegment(sketch, "E42.direction2", {"start": v(22.49, 55.98) * mm, "end": v(22.49, 44.3) * mm, "construction": true});
            skLineSegment(sketch, "E43.0.1.0", {"start": v(19.11, 30.83) * mm, "end": v(16.2, 26.67) * mm});
            skLineSegment(sketch, "E43.0.1.1", {"start": v(19.11, 30.83) * mm, "end": v(22.03, 26.67) * mm});
            skLineSegment(sketch, "E43.0.1.2", {"start": v(19.11, 22.5) * mm, "end": v(22.03, 26.67) * mm});
            skLineSegment(sketch, "E43.0.1.3", {"start": v(19.11, 22.5) * mm, "end": v(16.2, 26.67) * mm});
            skLineSegment(sketch, "E43.0.2.0", {"start": v(19.11, 42.51) * mm, "end": v(16.2, 38.35) * mm});
            skLineSegment(sketch, "E43.0.2.1", {"start": v(19.11, 42.51) * mm, "end": v(22.03, 38.35) * mm});
            skLineSegment(sketch, "E43.0.2.2", {"start": v(19.11, 34.19) * mm, "end": v(22.03, 38.35) * mm});
            skLineSegment(sketch, "E43.0.2.3", {"start": v(19.11, 34.19) * mm, "end": v(16.2, 38.35) * mm});
            skLineSegment(sketch, "E43.0.3.0", {"start": v(19.11, 54.2) * mm, "end": v(16.2, 50.03) * mm});
            skLineSegment(sketch, "E43.0.3.1", {"start": v(19.11, 54.2) * mm, "end": v(22.03, 50.03) * mm});
            skLineSegment(sketch, "E43.0.3.2", {"start": v(19.11, 45.87) * mm, "end": v(22.03, 50.03) * mm});
            skLineSegment(sketch, "E43.0.3.3", {"start": v(19.11, 45.87) * mm, "end": v(16.2, 50.03) * mm});
            skLineSegment(sketch, "E43.1.0.0", {"start": v(6.41, 19.14) * mm, "end": v(3.5, 14.98) * mm});
            skLineSegment(sketch, "E43.1.0.1", {"start": v(6.41, 19.14) * mm, "end": v(9.33, 14.98) * mm});
            skLineSegment(sketch, "E43.1.0.2", {"start": v(6.41, 10.82) * mm, "end": v(9.33, 14.98) * mm});
            skLineSegment(sketch, "E43.1.0.3", {"start": v(6.41, 10.82) * mm, "end": v(3.5, 14.98) * mm});
            skLineSegment(sketch, "E43.1.1.0", {"start": v(6.41, 30.83) * mm, "end": v(3.5, 26.67) * mm});
            skLineSegment(sketch, "E43.1.1.1", {"start": v(6.41, 30.83) * mm, "end": v(9.33, 26.67) * mm});
            skLineSegment(sketch, "E43.1.1.2", {"start": v(6.41, 22.5) * mm, "end": v(9.33, 26.67) * mm});
            skLineSegment(sketch, "E43.1.1.3", {"start": v(6.41, 22.5) * mm, "end": v(3.5, 26.67) * mm});
            skLineSegment(sketch, "E43.1.2.0", {"start": v(6.41, 42.51) * mm, "end": v(3.5, 38.35) * mm});
            skLineSegment(sketch, "E43.1.2.1", {"start": v(6.41, 42.51) * mm, "end": v(9.33, 38.35) * mm});
            skLineSegment(sketch, "E43.1.2.2", {"start": v(6.41, 34.19) * mm, "end": v(9.33, 38.35) * mm});
            skLineSegment(sketch, "E43.1.2.3", {"start": v(6.41, 34.19) * mm, "end": v(3.5, 38.35) * mm});
            skLineSegment(sketch, "E43.1.3.0", {"start": v(6.41, 54.2) * mm, "end": v(3.5, 50.03) * mm});
            skLineSegment(sketch, "E43.1.3.1", {"start": v(6.41, 54.2) * mm, "end": v(9.33, 50.03) * mm});
            skLineSegment(sketch, "E43.1.3.2", {"start": v(6.41, 45.87) * mm, "end": v(9.33, 50.03) * mm});
            skLineSegment(sketch, "E43.1.3.3", {"start": v(6.41, 45.87) * mm, "end": v(3.5, 50.03) * mm});
            skLineSegment(sketch, "E43.2.0.0", {"start": v(-6.29, 19.14) * mm, "end": v(-9.2, 14.98) * mm});
            skLineSegment(sketch, "E43.2.0.1", {"start": v(-6.29, 19.14) * mm, "end": v(-3.37, 14.98) * mm});
            skLineSegment(sketch, "E43.2.0.2", {"start": v(-6.29, 10.82) * mm, "end": v(-3.37, 14.98) * mm});
            skLineSegment(sketch, "E43.2.0.3", {"start": v(-6.29, 10.82) * mm, "end": v(-9.2, 14.98) * mm});
            skLineSegment(sketch, "E43.2.1.0", {"start": v(-6.29, 30.83) * mm, "end": v(-9.2, 26.67) * mm});
            skLineSegment(sketch, "E43.2.1.1", {"start": v(-6.29, 30.83) * mm, "end": v(-3.37, 26.67) * mm});
            skLineSegment(sketch, "E43.2.1.2", {"start": v(-6.29, 22.5) * mm, "end": v(-3.37, 26.67) * mm});
            skLineSegment(sketch, "E43.2.1.3", {"start": v(-6.29, 22.5) * mm, "end": v(-9.2, 26.67) * mm});
            skLineSegment(sketch, "E43.2.2.0", {"start": v(-6.29, 42.51) * mm, "end": v(-9.2, 38.35) * mm});
            skLineSegment(sketch, "E43.2.2.1", {"start": v(-6.29, 42.51) * mm, "end": v(-3.37, 38.35) * mm});
            skLineSegment(sketch, "E43.2.2.2", {"start": v(-6.29, 34.19) * mm, "end": v(-3.37, 38.35) * mm});
            skLineSegment(sketch, "E43.2.2.3", {"start": v(-6.29, 34.19) * mm, "end": v(-9.2, 38.35) * mm});
            skLineSegment(sketch, "E43.2.3.0", {"start": v(-6.29, 54.2) * mm, "end": v(-9.2, 50.03) * mm});
            skLineSegment(sketch, "E43.2.3.1", {"start": v(-6.29, 54.2) * mm, "end": v(-3.37, 50.03) * mm});
            skLineSegment(sketch, "E43.2.3.2", {"start": v(-6.29, 45.87) * mm, "end": v(-3.37, 50.03) * mm});
            skLineSegment(sketch, "E43.2.3.3", {"start": v(-6.29, 45.87) * mm, "end": v(-9.2, 50.03) * mm});
            skLineSegment(sketch, "E43.3.0.0", {"start": v(-18.99, 19.14) * mm, "end": v(-21.9, 14.98) * mm});
            skLineSegment(sketch, "E43.3.0.1", {"start": v(-18.99, 19.14) * mm, "end": v(-16.07, 14.98) * mm});
            skLineSegment(sketch, "E43.3.0.2", {"start": v(-18.99, 10.82) * mm, "end": v(-16.07, 14.98) * mm});
            skLineSegment(sketch, "E43.3.0.3", {"start": v(-18.99, 10.82) * mm, "end": v(-21.9, 14.98) * mm});
            skLineSegment(sketch, "E43.3.1.0", {"start": v(-18.99, 30.83) * mm, "end": v(-21.9, 26.67) * mm});
            skLineSegment(sketch, "E43.3.1.1", {"start": v(-18.99, 30.83) * mm, "end": v(-16.07, 26.67) * mm});
            skLineSegment(sketch, "E43.3.1.2", {"start": v(-18.99, 22.5) * mm, "end": v(-16.07, 26.67) * mm});
            skLineSegment(sketch, "E43.3.1.3", {"start": v(-18.99, 22.5) * mm, "end": v(-21.9, 26.67) * mm});
            skLineSegment(sketch, "E43.3.2.0", {"start": v(-18.99, 42.51) * mm, "end": v(-21.9, 38.35) * mm});
            skLineSegment(sketch, "E43.3.2.1", {"start": v(-18.99, 42.51) * mm, "end": v(-16.07, 38.35) * mm});
            skLineSegment(sketch, "E43.3.2.2", {"start": v(-18.99, 34.19) * mm, "end": v(-16.07, 38.35) * mm});
            skLineSegment(sketch, "E43.3.2.3", {"start": v(-18.99, 34.19) * mm, "end": v(-21.9, 38.35) * mm});
            skLineSegment(sketch, "E43.3.3.0", {"start": v(-18.99, 54.2) * mm, "end": v(-21.9, 50.03) * mm});
            skLineSegment(sketch, "E43.3.3.1", {"start": v(-18.99, 54.2) * mm, "end": v(-16.07, 50.03) * mm});
            skLineSegment(sketch, "E43.3.3.2", {"start": v(-18.99, 45.87) * mm, "end": v(-16.07, 50.03) * mm});
            skLineSegment(sketch, "E43.3.3.3", {"start": v(-18.99, 45.87) * mm, "end": v(-21.9, 50.03) * mm});
            skLineSegment(sketch, "E43.direction1", {"start": v(16.2, 14.98) * mm, "end": v(3.5, 14.98) * mm, "construction": true});
            skLineSegment(sketch, "E43.direction2", {"start": v(16.2, 14.98) * mm, "end": v(16.2, 26.67) * mm, "construction": true});
            skSolve(sketch);
        }
        {
            var Q0;
            Q0=makeQuery(id+"F12.imprint","IMPRINT",FACE,{"disambiguationData":[TD([[makeQuery(id+"F12.imprint","IMPRINT",EDGE,{"derivedFrom":sQuery(id+"F12.wireOp",EDGE,"E42.4.0.0")}),1.0]])]});
            var Q1;
            Q1=makeQuery(id+"F12.imprint","IMPRINT",FACE,{"disambiguationData":[TD([[makeQuery(id+"F12.imprint","IMPRINT",EDGE,{"derivedFrom":sQuery(id+"F12.wireOp",EDGE,"E42.3.0.0")}),1.0]])]});
            var Q2;
            Q2=makeQuery(id+"F12.imprint","IMPRINT",FACE,{"disambiguationData":[TD([[makeQuery(id+"F12.imprint","IMPRINT",EDGE,{"derivedFrom":sQuery(id+"F12.wireOp",EDGE,"E42.2.0.0")}),1.0]])]});
            var Q3;
            Q3=makeQuery(id+"F12.imprint","IMPRINT",FACE,{"disambiguationData":[TD([[makeQuery(id+"F12.imprint","IMPRINT",EDGE,{"derivedFrom":sQuery(id+"F12.wireOp",EDGE,"E41.2.4.0")}),1.0]])]});
            var Q4;
            Q4=makeQuery(id+"F12.imprint","IMPRINT",FACE,{"disambiguationData":[TD([[makeQuery(id+"F12.imprint","IMPRINT",EDGE,{"derivedFrom":sQuery(id+"F12.wireOp",EDGE,"E43.3.3.0")}),1.0]])]});
            var Q5;
            Q5=makeQuery(id+"F12.imprint","IMPRINT",FACE,{"disambiguationData":[TD([[makeQuery(id+"F12.imprint","IMPRINT",EDGE,{"derivedFrom":sQuery(id+"F12.wireOp",EDGE,"E43.2.3.0")}),1.0]])]});
            var Q6;
            Q6=makeQuery(id+"F12.imprint","IMPRINT",FACE,{"disambiguationData":[TD([[makeQuery(id+"F12.imprint","IMPRINT",EDGE,{"derivedFrom":sQuery(id+"F12.wireOp",EDGE,"E43.1.3.0")}),1.0]])]});
            var Q7;
            Q7=makeQuery(id+"F12.imprint","IMPRINT",FACE,{"disambiguationData":[TD([[makeQuery(id+"F12.imprint","IMPRINT",EDGE,{"derivedFrom":sQuery(id+"F12.wireOp",EDGE,"E43.0.3.0")}),1.0]])]});
            var Q8;
            Q8=makeQuery(id+"F12.imprint","IMPRINT",FACE,{"disambiguationData":[TD([[makeQuery(id+"F12.imprint","IMPRINT",EDGE,{"derivedFrom":sQuery(id+"F12.wireOp",EDGE,"E42.1.0.0")}),1.0]])]});
            var Q9;
            Q9=makeQuery(id+"F12.imprint","IMPRINT",FACE,{"disambiguationData":[TD([[makeQuery(id+"F12.imprint","IMPRINT",EDGE,{"derivedFrom":sQuery(id+"F12.wireOp",EDGE,"E42.4.1.0")}),1.0]])]});
            var Q10;
            Q10=makeQuery(id+"F12.imprint","IMPRINT",FACE,{"disambiguationData":[TD([[makeQuery(id+"F12.imprint","IMPRINT",EDGE,{"derivedFrom":sQuery(id+"F12.wireOp",EDGE,"E42.3.1.0")}),1.0]])]});
            var Q11;
            Q11=makeQuery(id+"F12.imprint","IMPRINT",FACE,{"disambiguationData":[TD([[makeQuery(id+"F12.imprint","IMPRINT",EDGE,{"derivedFrom":sQuery(id+"F12.wireOp",EDGE,"E42.2.1.0")}),1.0]])]});
            var Q12;
            Q12=makeQuery(id+"F12.imprint","IMPRINT",FACE,{"disambiguationData":[TD([[makeQuery(id+"F12.imprint","IMPRINT",EDGE,{"derivedFrom":sQuery(id+"F12.wireOp",EDGE,"E42.1.1.0")}),1.0]])]});
            var Q13;
            Q13=makeQuery(id+"F12.imprint","IMPRINT",FACE,{"disambiguationData":[TD([[makeQuery(id+"F12.imprint","IMPRINT",EDGE,{"derivedFrom":sQuery(id+"F12.wireOp",EDGE,"E42.0.1.0")}),1.0]])]});
            var Q14;
            Q14=makeQuery(id+"F12.imprint","IMPRINT",FACE,{"disambiguationData":[TD([[makeQuery(id+"F12.imprint","IMPRINT",EDGE,{"derivedFrom":sQuery(id+"F12.wireOp",EDGE,"E43.0.2.0")}),1.0]])]});
            var Q15;
            Q15=makeQuery(id+"F12.imprint","IMPRINT",FACE,{"disambiguationData":[TD([[makeQuery(id+"F12.imprint","IMPRINT",EDGE,{"derivedFrom":sQuery(id+"F12.wireOp",EDGE,"E43.1.2.0")}),1.0]])]});
            var Q16;
            Q16=makeQuery(id+"F12.imprint","IMPRINT",FACE,{"disambiguationData":[TD([[makeQuery(id+"F12.imprint","IMPRINT",EDGE,{"derivedFrom":sQuery(id+"F12.wireOp",EDGE,"E43.2.2.0")}),1.0]])]});
            var Q17;
            Q17=makeQuery(id+"F12.imprint","IMPRINT",FACE,{"disambiguationData":[TD([[makeQuery(id+"F12.imprint","IMPRINT",EDGE,{"derivedFrom":sQuery(id+"F12.wireOp",EDGE,"E43.3.2.0")}),1.0]])]});
            var Q18;
            Q18=makeQuery(id+"F12.imprint","IMPRINT",FACE,{"disambiguationData":[TD([[makeQuery(id+"F12.imprint","IMPRINT",EDGE,{"derivedFrom":sQuery(id+"F12.wireOp",EDGE,"E42.4.2.0")}),1.0]])]});
            var Q19;
            Q19=makeQuery(id+"F12.imprint","IMPRINT",FACE,{"disambiguationData":[TD([[makeQuery(id+"F12.imprint","IMPRINT",EDGE,{"derivedFrom":sQuery(id+"F12.wireOp",EDGE,"E42.3.2.0")}),1.0]])]});
            var Q20;
            Q20=makeQuery(id+"F12.imprint","IMPRINT",FACE,{"disambiguationData":[TD([[makeQuery(id+"F12.imprint","IMPRINT",EDGE,{"derivedFrom":sQuery(id+"F12.wireOp",EDGE,"E42.2.2.0")}),1.0]])]});
            var Q21;
            Q21=makeQuery(id+"F12.imprint","IMPRINT",FACE,{"disambiguationData":[TD([[makeQuery(id+"F12.imprint","IMPRINT",EDGE,{"derivedFrom":sQuery(id+"F12.wireOp",EDGE,"E42.0.2.0")}),1.0]])]});
            var Q22;
            Q22=makeQuery(id+"F12.imprint","IMPRINT",FACE,{"disambiguationData":[TD([[makeQuery(id+"F12.imprint","IMPRINT",EDGE,{"derivedFrom":sQuery(id+"F12.wireOp",EDGE,"E43.0.1.0")}),1.0]])]});
            var Q23;
            Q23=makeQuery(id+"F12.imprint","IMPRINT",FACE,{"disambiguationData":[TD([[makeQuery(id+"F12.imprint","IMPRINT",EDGE,{"derivedFrom":sQuery(id+"F12.wireOp",EDGE,"E43.1.1.0")}),1.0]])]});
            var Q24;
            Q24=makeQuery(id+"F12.imprint","IMPRINT",FACE,{"disambiguationData":[TD([[makeQuery(id+"F12.imprint","IMPRINT",EDGE,{"derivedFrom":sQuery(id+"F12.wireOp",EDGE,"E43.2.1.0")}),1.0]])]});
            var Q25;
            Q25=makeQuery(id+"F12.imprint","IMPRINT",FACE,{"disambiguationData":[TD([[makeQuery(id+"F12.imprint","IMPRINT",EDGE,{"derivedFrom":sQuery(id+"F12.wireOp",EDGE,"E42.4.3.0")}),1.0]])]});
            var Q26;
            Q26=makeQuery(id+"F12.imprint","IMPRINT",FACE,{"disambiguationData":[TD([[makeQuery(id+"F12.imprint","IMPRINT",EDGE,{"derivedFrom":sQuery(id+"F12.wireOp",EDGE,"E42.3.3.0")}),1.0]])]});
            var Q27;
            Q27=makeQuery(id+"F12.imprint","IMPRINT",FACE,{"disambiguationData":[TD([[makeQuery(id+"F12.imprint","IMPRINT",EDGE,{"derivedFrom":sQuery(id+"F12.wireOp",EDGE,"E42.2.3.0")}),1.0]])]});
            var Q28;
            Q28=makeQuery(id+"F12.imprint","IMPRINT",FACE,{"disambiguationData":[TD([[makeQuery(id+"F12.imprint","IMPRINT",EDGE,{"derivedFrom":sQuery(id+"F12.wireOp",EDGE,"E42.1.3.0")}),1.0]])]});
            var Q29;
            Q29=makeQuery(id+"F12.imprint","IMPRINT",FACE,{"disambiguationData":[TD([[makeQuery(id+"F12.imprint","IMPRINT",EDGE,{"derivedFrom":sQuery(id+"F12.wireOp",EDGE,"E42.0.3.0")}),1.0]])]});
            var Q30;
            Q30=makeQuery(id+"F12.imprint","IMPRINT",FACE,{"disambiguationData":[TD([[makeQuery(id+"F12.imprint","IMPRINT",EDGE,{"derivedFrom":sQuery(id+"F12.wireOp",EDGE,"E43.3.0.0")}),1.0]])]});
            var Q31;
            Q31=makeQuery(id+"F12.imprint","IMPRINT",FACE,{"disambiguationData":[TD([[makeQuery(id+"F12.imprint","IMPRINT",EDGE,{"derivedFrom":sQuery(id+"F12.wireOp",EDGE,"E43.2.0.0")}),1.0]])]});
            var Q32;
            Q32=makeQuery(id+"F12.imprint","IMPRINT",FACE,{"disambiguationData":[TD([[makeQuery(id+"F12.imprint","IMPRINT",EDGE,{"derivedFrom":sQuery(id+"F12.wireOp",EDGE,"E42.0.4.0")}),1.0]])]});
            var Q33;
            Q33=makeQuery(id+"F12.imprint","IMPRINT",FACE,{"disambiguationData":[TD([[makeQuery(id+"F12.imprint","IMPRINT",EDGE,{"derivedFrom":sQuery(id+"F12.wireOp",EDGE,"E42.1.4.0")}),1.0]])]});
            var Q34;
            Q34=makeQuery(id+"F12.imprint","IMPRINT",FACE,{"disambiguationData":[TD([[makeQuery(id+"F12.imprint","IMPRINT",EDGE,{"derivedFrom":sQuery(id+"F12.wireOp",EDGE,"E42.2.4.0")}),1.0]])]});
            var Q35;
            Q35=makeQuery(id+"F12.imprint","IMPRINT",FACE,{"disambiguationData":[TD([[makeQuery(id+"F12.imprint","IMPRINT",EDGE,{"derivedFrom":sQuery(id+"F12.wireOp",EDGE,"E42.3.4.0")}),1.0]])]});
            var Q36;
            Q36=makeQuery(id+"F12.imprint","IMPRINT",FACE,{"disambiguationData":[TD([[makeQuery(id+"F12.imprint","IMPRINT",EDGE,{"derivedFrom":sQuery(id+"F12.wireOp",EDGE,"E43.1.0.0")}),1.0]])]});
            var Q37;
            Q37=makeQuery(id+"F12.imprint","IMPRINT",FACE,{"disambiguationData":[TD([[makeQuery(id+"F12.imprint","IMPRINT",EDGE,{"derivedFrom":sQuery(id+"F12.wireOp",EDGE,"E42.1.2.0")}),1.0]])]});
            var Q38;
            Q38=makeQuery(id+"F12.imprint","IMPRINT",FACE,{"disambiguationData":[TD([[makeQuery(id+"F12.imprint","IMPRINT",EDGE,{"derivedFrom":sQuery(id+"F12.wireOp",EDGE,"E43.3.1.0")}),1.0]])]});
            extrude(context, id + "F13", {"entities" : qUnion([Q0, Q1, Q2, Q3, Q4, Q5, Q6, Q7, Q8, Q9, Q10, Q11, Q12, Q13, Q14, Q15, Q16, Q17, Q18, Q19, Q20, Q21, Q22, Q23, Q24, Q25, Q26, Q27, Q28, Q29, Q30, Q31, Q32, Q33, Q34, Q35, Q36, Q37, Q38]), "operationType" : NewBodyOperationType.REMOVE, "oppositeDirection" : true, "depth" : 25.4 * mm, "offsetDistance" : 25.4 * mm});
        }
        {
            var Q0;
            Q0=makeQuery(id+"F3.opExtrude","CAP_FACE",FACE,{"disambiguationData":[OSD([sQuery(id+"F2.wireOp",EDGE,"E11.bottom"),sQuery(id+"F2.wireOp",EDGE,"E11.top"),sQuery(id+"F2.wireOp",EDGE,"E11.left"),sQuery(id+"F2.wireOp",EDGE,"E11.right")])],"isStart":false});
            var Q1;
            Q1=makeQuery(id+"F3.boolean.opBoolean","MERGE",FACE,{"derivedFrom":[makeQuery(id+"F1.opExtrude","SWEPT_FACE",FACE,{"disambiguationData":[OSD([sQuery(id+"F0.wireOp",EDGE,"E4"),sQuery(id+"F0.wireOp",EDGE,"E8.MirrorCS")])]}),makeQuery(id+"F3.opExtrude","SWEPT_FACE",FACE,{"disambiguationData":[OSD([sQuery(id+"F2.wireOp",EDGE,"E11.top")])]})]});
            var Q2;
            Q2=makeQuery(id+"F3.boolean.opBoolean","MERGE",FACE,{"derivedFrom":[makeQuery(id+"F1.opExtrude","SWEPT_FACE",FACE,{"disambiguationData":[OSD([sQuery(id+"F0.wireOp",EDGE,"E9.MirrorCS")])]}),makeQuery(id+"F3.opExtrude","SWEPT_FACE",FACE,{"disambiguationData":[OSD([sQuery(id+"F2.wireOp",EDGE,"E11.left")])]})]});
            var Q3;
            Q3=makeQuery(id+"F1.opExtrude","SWEPT_FACE",FACE,{"disambiguationData":[OSD([sQuery(id+"F0.wireOp",EDGE,"E6.MirrorCS")])]});
            var Q4;
            Q4=makeQuery(id+"F3.boolean.opBoolean","MERGE",FACE,{"derivedFrom":[makeQuery(id+"F1.opExtrude","SWEPT_FACE",FACE,{"disambiguationData":[OSD([sQuery(id+"F0.wireOp",EDGE,"E3")])]}),makeQuery(id+"F3.opExtrude","SWEPT_FACE",FACE,{"disambiguationData":[OSD([sQuery(id+"F2.wireOp",EDGE,"E11.right")])]})]});
            var Q5;
            Q5=makeQuery(id+"F1.opExtrude","SWEPT_FACE",FACE,{"disambiguationData":[OSD([sQuery(id+"F0.wireOp",EDGE,"E1")])]});
            fillet(context, id + "F14", {"entities" : qUnion([Q0, Q1, Q2, Q3, Q4, Q5]), "radius" : 0.5 * mm, "tangentPropagation" : true, "allowEdgeOverflow" : false});
        }
        {
            var Q0;
            Q0=makeQuery(id+"F1.opExtrude","CAP_EDGE",EDGE,{"disambiguationData":[OSD([sQuery(id+"F0.wireOp",EDGE,"E10.MirrorCS")])],"isStart":true});
            var Q1;
            Q1=makeQuery(id+"F1.opExtrude","CAP_EDGE",EDGE,{"disambiguationData":[OSD([sQuery(id+"F0.wireOp",EDGE,"E2")])],"isStart":true});
            fillet(context, id + "F15", {"entities" : qUnion([Q0, Q1]), "radius" : 5.08 * mm, "tangentPropagation" : true, "allowEdgeOverflow" : false});
        }
        {
            var Q0;
            Q0=makeQuery(id+"F3.opExtrude","CAP_FACE",FACE,{"disambiguationData":[OSD([sQuery(id+"F2.wireOp",EDGE,"E11.bottom"),sQuery(id+"F2.wireOp",EDGE,"E11.top"),sQuery(id+"F2.wireOp",EDGE,"E11.left"),sQuery(id+"F2.wireOp",EDGE,"E11.right")])],"isStart":true});
            fillet(context, id + "F16", {"entities" : qUnion([Q0]), "radius" : 0.5 * mm, "tangentPropagation" : true, "allowEdgeOverflow" : false});
        }
    });
